# Revit family: Qmax 700.rfa(Shrd)
name_source: partatom
category: Plumbing Fixtures
revit_build: Autodesk Revit 2013 (Build: 20120221_2030(x64)
units: mm (PartAtom-declared; Revit-internal decimal feet)

## types (5) — shared parameters
550-700 Step Connector - Colour = Black
550-700 Step Connector - Dimensions = 730mm x 45mm x 865mm (LxWxH)
550-700 Step Connector - Material = High Density Polyethylene
550-700 Step Connector - Model Description = High capacity slot drainage channel system
550-700 Step Connector - Product Code = 32882
550-700 Step Connector - Recyclable = Fully recyclable
550-700 Step Connector - Recycled Material Content = 0%
550-700 Step Connector - Weight = 2.5 kg
ACO Hydraulic Design Software = http://www.acodesign.co.uk
Assembly Code = D2040
Chamber Connector - Channel Colour = Black
Chamber Connector - Channel Material = Medium Density Polyethylene
Chamber Connector - Dimensions = Female End=800mm x 715mm x 895mm, Male End=800mm x 715mm x 845mm  (LxWxH)
Chamber Connector - Model Description = High capacity slot drainage channel system
Chamber Connector - Product Code = 32854
Chamber Connector - Recyclable = Fully recyclable
Chamber Connector - Recycled Material Content = Variable %
Chamber Connector - Weight = 15.8 kg
Channel C.S.A = 249703mm²
Channel Colour = Black
Channel Material = Medium Density Polyethylene
Channel Recyclable = Fully recyclable
Channel Recycled Material Content = Variable %
Closing End Cap - Colour = Black
Closing End Cap - Dimensions = 730mm x 12mm x 865mm (LxWxH)
Closing End Cap - Material = High Density Polyethylene
Closing End Cap - Model Description = High capacity slot drainage channel system
Closing End Cap - Product Code = 32835
Closing End Cap - Recyclable = Fully recyclable
Closing End Cap - Recycled Material Content = 0%
Closing End Cap - Weight = 4.9 kg
Concrete Surround Volume - Load Class A 15 - D 400 = 0.56 m³/m
Concrete Surround Volume - Load Class E 600 - F 900 = 0.72 m³/m
Edge Rail Recyclable = Fully recyclable
Edge Rail Recycled Material Content = Between 40% - 90%
Fax = +44 (0)1462 815895
Installation - Concrete Grade = Refer to brochure
Installation - Reinforcement Details = Refer to brochure
Installation Guidelines = http://www.aco.co.uk
Length = 2000 mm  [stored 6.56168 ft]
Load Class = A 15 - F 900
Maintenance Guidelines = http://www.aco.co.uk
Manufacturer = ACO Technologies plc - ACO Water Management Division
Model = ACO Qmax 700
Model Description = High capacity slot drainage channel system
Price = POA - contact ACO
Product Brochure = http://www.aco.co.uk
Product Page URL = http://www.aco.co.uk
Product Standard = BS EN 1433:2002 CE  marked
Revision = 1
Seal Colour = Black
Seal Material = EPDM
Seal Recyclable = Fully recyclable
Seal Recycled Material Content = 0%
Telephone = +44 (0)1462 816666
URL = www.aco.co.uk
Width Overall = 730 mm  [stored 2.39501 ft]
zero-valued in all types: Cost, SerialNumber, TagNumber

## per-type parameters (varying)
| type | ChamberOrigin | ClosingEndCapOrigin | Depth Overall | Drainage Slot Intake Area | Drainage Slot Width | E1-QFlow-DuctileIron | E2-QGuard-DuctileIron | E3-QFlow-GalvSteel | E4-QGuard-GalvSteel | E5-QSlot-GalvSteel | Edge Rail Colour | Edge Rail Finish | Edge Rail Material | Floor Opening Width | Hydraulic Performance | Invert Depth | Material | Product Code | Product Dimensions | Product Weight | StepConn-Origin | Type Comments | V_CoarseE1 | V_Coarse_E5 |
| 32830 - Q-Flow Edge - D.I | 480 mm  [stored 1.5748 ft] | 571.607 mm  [stored 1.87535 ft] | 1070 mm  [stored 3.5105 ft] | 10000mm²/m | 10mm | Yes | No | No | No | No | Silver | Galvanised | Steel | 65 mm  [stored 0.213255 ft] | http://www.aco.co.uk | 1050mm | Iron, Ductile | 32834 | 2000mm x 730mm x 1170mm (LxWxH) | 47 kg | 581.655 mm  [stored 1.90832 ft] | ACO Qmax 700 channel assembly complete with ACO Q-Slot galvanised steel edge rail | Yes | No |
| 32831 - Q-Guard Edge - D.I | 480 mm  [stored 1.5748 ft] | 571.607 mm  [stored 1.87535 ft] | 1070 mm  [stored 3.5105 ft] | 10925mm²/m | 8mm twin slot | No | Yes | No | No | No | Black | ATec coating | Ductile Iron | 65 mm  [stored 0.213255 ft] | http://www.aco.co.uk
http://www.acodesign.co.uk | 950mm | Iron, Ductile | 32831 | 2000mm x 730mm x 1070mm (LxWxH) | 50.7 kg | 581.655 mm  [stored 1.90832 ft] | ACO Qmax 700 channel assembly complete with ACO Q-Guard ductile iron edge rail | Yes | No |
| 32832 - Q-Flow Edge - G.S | 480 mm  [stored 1.5748 ft] | 571.607 mm  [stored 1.87535 ft] | 1070 mm  [stored 3.5105 ft] | 18106mm²/m | 26mm | No | No | Yes | No | No | Silver
Silver | Galvanised | Steel | 90 mm  [stored 0.295276 ft] | http://www.aco.co.uk | 950mm | Steel, Galvanized | 32832 | 2000mm x 730mm x 1070mm (LxWxH) | 41.9 kg | 581.655 mm  [stored 1.90832 ft] | ACO Qmax 700 channel assembly complete with ACO Q-Flow galvanised steel edge rail | Yes | No |
| 32833 - Q-Guard Edge - G.S | 480 mm  [stored 1.5748 ft] | 571.607 mm  [stored 1.87535 ft] | 1070 mm  [stored 3.5105 ft] | 8356mm²/m | 10mm | No | No | No | Yes | No | Silver | Galvanised | Steel | 55 mm  [stored 0.180446 ft] | http://www.aco.co.uk | 950mm | Steel, Galvanized | 32833 | 2000mm x 730mm x 1070mm (LxWxH) | 39.4 kg | 581.655 mm  [stored 1.90832 ft] | ACO Qmax 700 channel assembly complete with ACO Q-Guard galvanised steel edge rail | Yes | No |
| 32834 - Q-Slot Edge - G.S | 580 mm  [stored 1.90289 ft] | 671.607 mm | 1170 mm  [stored 3.83858 ft] | 10000mm²/m | 10mm | No | No | No | No | Yes | Silver | Galvanised | Steel | 18 mm  [stored 0.0590551 ft] | http://www.aco.co.uk | 1050mm | Steel, Galvanized | 32834 | 2000mm x 730mm x 1170mm (LxWxH) | 47 kg | 681.655 mm | ACO Qmax 700 channel assembly complete with ACO Q-Slot galvanised steel edge rail | No | Yes |

note: [stored X ft] marks values corroborated as IEEE doubles in the binary element streams (Revit-internal decimal feet)

## geometry (parser evidence)
native form markers: Blend x4, Sweep x13
no freeform markers — native parametric forms only
